# Revit family: RN 26015 Umstell-Kugelhahn
name_source: partatom
category: Rohrzubehör
units: mm (PartAtom-declared; Revit-internal decimal feet)

## family parameters
Arbeitsebenenbasiert = Nein
Beim Laden mit Abzugskörper schneiden = Nein
Bemaßung runder Anschluss = Durchmesser verwenden
Gemeinsam genutzt = Nein
Immer vertikal = Ja
Teiletyp = Ventil - Zerlegung in

## types (6) — shared parameters
1.010.00.2 Number of the part of the guideline = 2
1.010.00.3 Issue date (month) of the guideline = 201601
1.010.00.4 Manufacturer name = R. Nussbaum AG
1.010.00.5 Revision date of the file = 20190514
1.100.00.3 Sort number for display sequence = 4
1.100.00.4 Product designation = Absperr- und Regelarmaturen
1.960/3L.00.8 Link (URL) = https://www.nussbaum.ch
2.700.00.4 valve assembly type = 11
2.700.00.7 maximum operating temperature TB [°C] = 100
2.700.00.8 maximum operating pressure(working pressure) ps [1.0 · 102 Pa] = 16
Connector Visibility = Nein
EnclosingSpace Visibility = Nein
Hersteller = R. Nussbauzm AG
Modell = 0
URL = https://www.nussbaum.ch

## per-type parameters (varying)
- DN 15: 1.800.00.3 BS number=0040140000000000000000000000010010000000000000000300000000; 1.810.00.3 Manufacturer’s reference number=26015.54; 1.810.00.4 DATANORM number=26015.54; 1.810.00.5 StLB number=655.173; 1.810.00.6 GTIN number=7612945676702; 2.700.00.26 product description=26015.54, Umstell-Kugelhahn, DN=15, Rp=½; 2.700.00.5 nominal size DN=15; 2.700.00.6 kvs-value [m3/h]=35; CONNECTOR0_DIAMETER_dX_0r=15 mm  [stored 0.0492126 ft]; CONNECTOR0_dX_00=40 mm; CONNECTOR0_dX_01=29 mm; CONNECTOR0_ref_dX=29 mm; CONNECTOR1_DIAMETER_dX_0r=15 mm  [stored 0.0492126 ft]; CONNECTOR1_dX_00=29 mm; CONNECTOR1_dX_01=40 mm; CONNECTOR1_ref_dX=29 mm; CONNECTOR2_DIAMETER_dY_0r=15 mm  [stored 0.0492126 ft]; CONNECTOR2_dY_00=40 mm; CONNECTOR2_dY_01=29 mm; CONNECTOR2_ref_dY=29 mm; R. Nussbaum AG 26015.54 en Visibility=Ja; R. Nussbaum AG 26015.55 en Visibility=Nein; R. Nussbaum AG 26015.56 en Visibility=Nein; R. Nussbaum AG 26015.57 en Visibility=Nein; R. Nussbaum AG 26015.58 en Visibility=Nein; R. Nussbaum AG 26015.59 en Visibility=Nein; Typenkommentare=AbsperrventilDN 15
- DN 20: 1.800.00.3 BS number=0040140000000000000000000000010010000000000000000400000000; 1.810.00.3 Manufacturer’s reference number=26015.55; 1.810.00.4 DATANORM number=26015.55; 1.810.00.5 StLB number=655.174; 1.810.00.6 GTIN number=7612945676726; 2.700.00.26 product description=26015.55, Umstell-Kugelhahn, DN=20, Rp=¾; 2.700.00.5 nominal size DN=20; 2.700.00.6 kvs-value [m3/h]=47; CONNECTOR0_DIAMETER_dX_0r=20 mm; CONNECTOR0_dX_00=45 mm; CONNECTOR0_dX_01=33 mm; CONNECTOR0_ref_dX=33 mm; CONNECTOR1_DIAMETER_dX_0r=20 mm; CONNECTOR1_dX_00=33 mm; CONNECTOR1_dX_01=45 mm; CONNECTOR1_ref_dX=33 mm; CONNECTOR2_DIAMETER_dY_0r=20 mm; CONNECTOR2_dY_00=45 mm; CONNECTOR2_dY_01=33 mm; CONNECTOR2_ref_dY=33 mm; R. Nussbaum AG 26015.54 en Visibility=Nein; R. Nussbaum AG 26015.55 en Visibility=Ja; R. Nussbaum AG 26015.56 en Visibility=Nein; R. Nussbaum AG 26015.57 en Visibility=Nein; R. Nussbaum AG 26015.58 en Visibility=Nein; R. Nussbaum AG 26015.59 en Visibility=Nein; Typenkommentare=AbsperrventilDN 20
- DN 25: 1.800.00.3 BS number=0040140000000000000000000000010010000000000000000500000000; 1.810.00.3 Manufacturer’s reference number=26015.56; 1.810.00.4 DATANORM number=26015.56; 1.810.00.5 StLB number=655.175; 1.810.00.6 GTIN number=7612945676740; 2.700.00.26 product description=26015.56, Umstell-Kugelhahn, DN=25, Rp=1; 2.700.00.5 nominal size DN=25; 2.700.00.6 kvs-value [m3/h]=54; CONNECTOR0_DIAMETER_dX_0r=25 mm  [stored 0.082021 ft]; CONNECTOR0_dX_00=53 mm; CONNECTOR0_dX_01=40 mm; CONNECTOR0_ref_dX=40 mm; CONNECTOR1_DIAMETER_dX_0r=25 mm  [stored 0.082021 ft]; CONNECTOR1_dX_00=40 mm; CONNECTOR1_dX_01=53 mm; CONNECTOR1_ref_dX=40 mm; CONNECTOR2_DIAMETER_dY_0r=25 mm  [stored 0.082021 ft]; CONNECTOR2_dY_00=53 mm; CONNECTOR2_dY_01=40 mm; CONNECTOR2_ref_dY=40 mm; R. Nussbaum AG 26015.54 en Visibility=Nein; R. Nussbaum AG 26015.55 en Visibility=Nein; R. Nussbaum AG 26015.56 en Visibility=Ja; R. Nussbaum AG 26015.57 en Visibility=Nein; R. Nussbaum AG 26015.58 en Visibility=Nein; R. Nussbaum AG 26015.59 en Visibility=Nein; Typenkommentare=AbsperrventilDN 25
- DN 32: 1.800.00.3 BS number=0040140000000000000000000000010010000000000000000600000000; 1.810.00.3 Manufacturer’s reference number=26015.57; 1.810.00.4 DATANORM number=26015.57; 1.810.00.5 StLB number=655.176; 1.810.00.6 GTIN number=7612945676764; 2.700.00.26 product description=26015.57, Umstell-Kugelhahn, DN=32, Rp=1¼; 2.700.00.5 nominal size DN=32; 2.700.00.6 kvs-value [m3/h]=82; CONNECTOR0_DIAMETER_dX_0r=32 mm; CONNECTOR0_dX_00=58 mm; CONNECTOR0_dX_01=45 mm; CONNECTOR0_ref_dX=45 mm; CONNECTOR1_DIAMETER_dX_0r=32 mm; CONNECTOR1_dX_00=45 mm; CONNECTOR1_dX_01=58 mm; CONNECTOR1_ref_dX=45 mm; CONNECTOR2_DIAMETER_dY_0r=32 mm; CONNECTOR2_dY_00=58 mm; CONNECTOR2_dY_01=45 mm; CONNECTOR2_ref_dY=45 mm; R. Nussbaum AG 26015.54 en Visibility=Nein; R. Nussbaum AG 26015.55 en Visibility=Nein; R. Nussbaum AG 26015.56 en Visibility=Nein; R. Nussbaum AG 26015.57 en Visibility=Ja; R. Nussbaum AG 26015.58 en Visibility=Nein; R. Nussbaum AG 26015.59 en Visibility=Nein; Typenkommentare=AbsperrventilDN 32
- DN 40: 1.800.00.3 BS number=0040140000000000000000000000010010000000000000000700000000; 1.810.00.3 Manufacturer’s reference number=26015.58; 1.810.00.4 DATANORM number=26015.58; 1.810.00.5 StLB number=655.177; 1.810.00.6 GTIN number=7612945676788; 2.700.00.26 product description=26015.58, Umstell-Kugelhahn, DN=40, Rp=1½; 2.700.00.5 nominal size DN=40; 2.700.00.6 kvs-value [m3/h]=160; CONNECTOR0_DIAMETER_dX_0r=40 mm; CONNECTOR0_dX_00=69 mm; CONNECTOR0_dX_01=54 mm; CONNECTOR0_ref_dX=54 mm; CONNECTOR1_DIAMETER_dX_0r=40 mm; CONNECTOR1_dX_00=54 mm; CONNECTOR1_dX_01=69 mm; CONNECTOR1_ref_dX=54 mm; CONNECTOR2_DIAMETER_dY_0r=40 mm; CONNECTOR2_dY_00=69 mm; CONNECTOR2_dY_01=54 mm; CONNECTOR2_ref_dY=54 mm; R. Nussbaum AG 26015.54 en Visibility=Nein; R. Nussbaum AG 26015.55 en Visibility=Nein; R. Nussbaum AG 26015.56 en Visibility=Nein; R. Nussbaum AG 26015.57 en Visibility=Nein; R. Nussbaum AG 26015.58 en Visibility=Ja; R. Nussbaum AG 26015.59 en Visibility=Nein; Typenkommentare=AbsperrventilDN 40
- DN 50: 1.800.00.3 BS number=0040140000000000000000000000010010000000000000000800000000; 1.810.00.3 Manufacturer’s reference number=26015.59; 1.810.00.4 DATANORM number=26015.59; 1.810.00.5 StLB number=655.178; 1.810.00.6 GTIN number=7612945676801; 2.700.00.26 product description=26015.59, Umstell-Kugelhahn, DN=50, Rp=2; 2.700.00.5 nominal size DN=50; 2.700.00.6 kvs-value [m3/h]=230; CONNECTOR0_DIAMETER_dX_0r=50 mm; CONNECTOR0_dX_00=81 mm; CONNECTOR0_dX_01=64 mm; CONNECTOR0_ref_dX=64 mm; CONNECTOR1_DIAMETER_dX_0r=50 mm; CONNECTOR1_dX_00=64 mm; CONNECTOR1_dX_01=81 mm; CONNECTOR1_ref_dX=64 mm; CONNECTOR2_DIAMETER_dY_0r=50 mm; CONNECTOR2_dY_00=81 mm; CONNECTOR2_dY_01=64 mm; CONNECTOR2_ref_dY=64 mm; R. Nussbaum AG 26015.54 en Visibility=Nein; R. Nussbaum AG 26015.55 en Visibility=Nein; R. Nussbaum AG 26015.56 en Visibility=Nein; R. Nussbaum AG 26015.57 en Visibility=Nein; R. Nussbaum AG 26015.58 en Visibility=Nein; R. Nussbaum AG 26015.59 en Visibility=Ja; Typenkommentare=AbsperrventilDN 50

note: [stored X ft] marks values corroborated as IEEE doubles in the binary element streams (Revit-internal decimal feet)

## geometry (parser evidence)
native form markers: Sweep x1
no freeform markers — native parametric forms only
